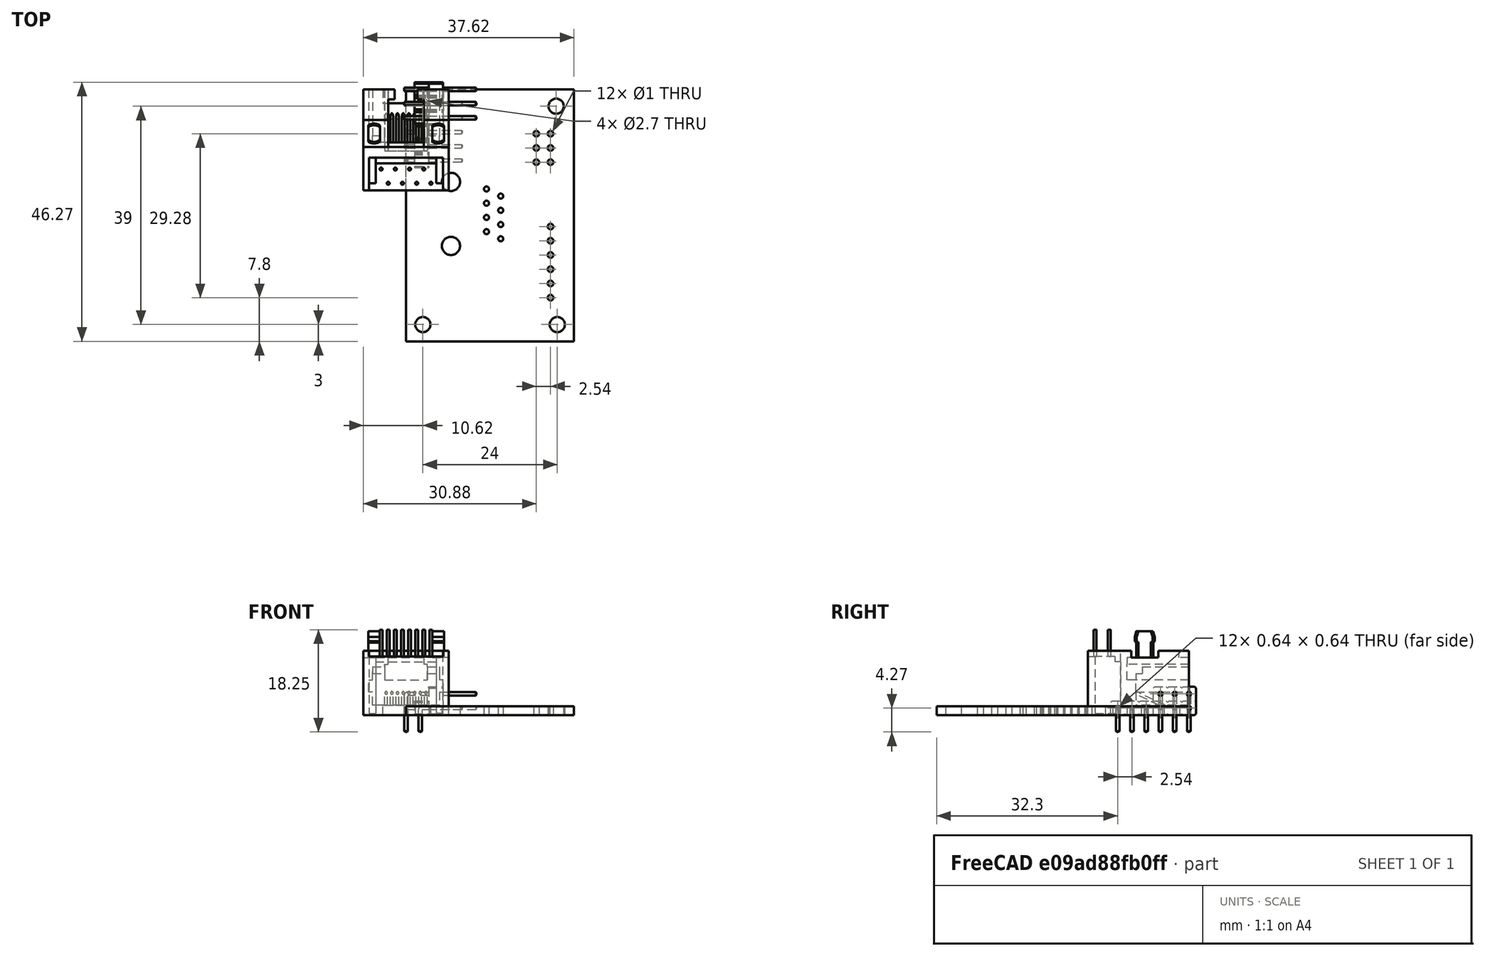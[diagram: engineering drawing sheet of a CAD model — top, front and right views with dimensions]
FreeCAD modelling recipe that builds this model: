
FCSTD DOCUMENT  (FreeCAD 0.21R33771 (Git))
Label: lsx-1
License: All rights reserved
LicenseURL: http://en.wikipedia.org/wiki/All_rights_reserved
objects: Part::Feature×4, App::Part×4, PartDesign::ShapeBinder×4, PartDesign::Point×4, Sketcher::SketchObject×1, PartDesign::Pad×1, PartDesign::Body×1
note: 16 computed .brp shape members not serialized (recipe doc carries the construction recipe); baked Part::Feature solids carry a one-line shape summary decoded from their .brp

FEATURE [Part::Feature] Part__Feature  label="54601-908WPLF"
  shape: bbox 15.24 x 18 x 15.25 mm, 132 faces (baked)
FEATURE [App::Part] s54601_908wplf  label="s54601-908wplf"
  Group = -> [Part__Feature]
  Origin = -> Origin
  Placement = pos=(0.16,-22.28,13.15) rot=(-0.707107,0.707107,0;3.14159rad)
FEATURE [Part::Feature] Part__Feature001  label="PinHeader_1x06_P254mm_Horizontal"
  shape: bbox 10.36 x 15.24 x 5.54 mm, 166 faces (baked)
FEATURE [App::Part] PinHeader_1x06_P2_54mm_Horizontal  label="PinHeader_1x06_P2.54mm_Horizontal"
  Group = -> [Part__Feature001]
  Origin = -> Origin001
  Placement = pos=(25.8,-24.5,1.65) rot=(0,0,1;0rad)
FEATURE [Part::Feature] Part__Feature002  label="PinHeader_2x03_P254mm_Horizontal"
  shape: bbox 12.9 x 7.62 x 8.08 mm, 148 faces (baked)
FEATURE [App::Part] PinHeader_2x03_P2_54mm_Horizontal  label="PinHeader_2x03_P2.54mm_Horizontal"
  Group = -> [Part__Feature002]
  Origin = -> Origin002
  Placement = pos=(23.26,-7.92,1.65) rot=(0,0,1;0rad)
FEATURE [Part::Feature] Part__Feature003  label="lsx-1_PCB"
  shape: bbox 30 x 45 x 1.6 mm, 32 faces (baked)
FEATURE [App::Part] lsx_1_1  label="lsx-1 1"
  Group = -> [s54601_908wplf,PinHeader_1x06_P2_54mm_Horizontal,PinHeader_2x03_P2_54mm_Horizontal,Part__Feature003]
  Origin = -> Origin003
FEATURE [PartDesign::ShapeBinder] CopyPart__Feature003
  TraceSupport = false
FEATURE [PartDesign::Point] DatumPoint
  AttacherType = Attacher::AttachEnginePoint
  MapMode = 37
  Placement = pos=(30,-45,0) rot=(0,0,1;0rad)
  Support = -> [CopyPart__Feature003]
FEATURE [PartDesign::ShapeBinder] CopyPart__Feature004
  TraceSupport = false
FEATURE [PartDesign::Point] DatumPoint001
  AttacherType = Attacher::AttachEnginePoint
  MapMode = 37
  Placement = pos=(30,0,0) rot=(0,0,1;0rad)
  Support = -> [CopyPart__Feature004]
FEATURE [PartDesign::ShapeBinder] CopyPart__Feature005
  TraceSupport = false
FEATURE [PartDesign::Point] DatumPoint002
  AttacherType = Attacher::AttachEnginePoint
  MapMode = 37
  Placement = pos=(0,-45,0) rot=(0,0,1;0rad)
  Support = -> [CopyPart__Feature005]
FEATURE [PartDesign::ShapeBinder] CopyPart__Feature006
  TraceSupport = false
FEATURE [PartDesign::Point] DatumPoint003
  AttacherType = Attacher::AttachEnginePoint
  MapMode = 37
  Support = -> [CopyPart__Feature006]
FEATURE [Sketcher::SketchObject] Sketch
  FullyConstrained = false
  MapMode = 5
  Support = -> [XY_Plane004]
  sketch-geometry (8):
    g0: LineSegment StartX=0 StartY=0 StartZ=0 EndX=30.2829 EndY=0 EndZ=0
    g1: LineSegment StartX=30.2829 StartY=0 StartZ=0 EndX=30.2829 EndY=-44.717 EndZ=0
    g2: LineSegment StartX=30.2829 StartY=-44.717 StartZ=0 EndX=0 EndY=-44.717 EndZ=0
    g3: LineSegment StartX=0 StartY=-44.717 StartZ=0 EndX=0 EndY=0 EndZ=0
    g4: LineSegment StartX=-2 StartY=2 StartZ=0 EndX=30.7829 EndY=2 EndZ=0
    g5: LineSegment StartX=30.7829 StartY=2 StartZ=0 EndX=30.7829 EndY=-46.717 EndZ=0
    g6: LineSegment StartX=30.7829 StartY=-46.717 StartZ=0 EndX=-2 EndY=-46.717 EndZ=0
    g7: LineSegment StartX=-2 StartY=-46.717 StartZ=0 EndX=-2 EndY=2 EndZ=0
  constraints (21):
    c: Coincident(g0,g1)
    c: Coincident(g1,g2)
    c: Coincident(g2,g3)
    c: Coincident(g3,g0)
    c: Horizontal(g0)
    c: Horizontal(g2)
    c: Vertical(g1)
    c: Vertical(g3)
    c: Coincident(g0,g-1)
    c: Coincident(g4,g5)
    c: Coincident(g5,g6)
    c: Coincident(g6,g7)
    c: Coincident(g7,g4)
    c: Horizontal(g4)
    c: Horizontal(g6)
    c: Vertical(g5)
    c: Vertical(g7)
    c: Distance(g0,g7) = 2
    c: Distance(g0,g5) = 0.5
    c: Distance(g0,g4) = 2
    c: Distance(g2,g6) = 2
FEATURE [PartDesign::Pad] Pad
  Direction = (0,0,1)
  Length = 15
  Length2 = 10
  Profile = -> Sketch
  ReferenceAxis = -> Sketch [N_Axis]
  Type = 0
FEATURE [PartDesign::Body] Body
  Group = -> [DatumPoint,CopyPart__Feature003,DatumPoint001,CopyPart__Feature004,DatumPoint002,CopyPart__Feature005,DatumPoint003,CopyPart__Feature006,Sketch,Pad]
  Origin = -> Origin004
  Tip = -> Pad
